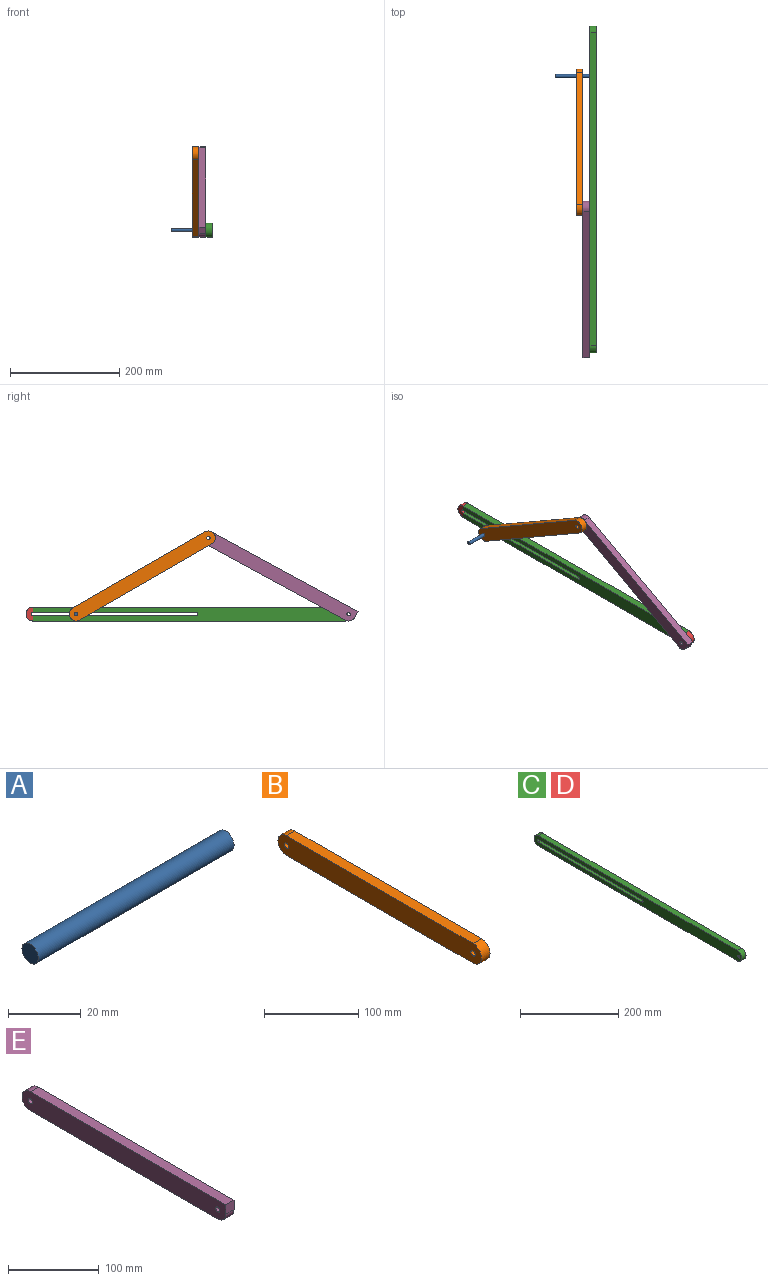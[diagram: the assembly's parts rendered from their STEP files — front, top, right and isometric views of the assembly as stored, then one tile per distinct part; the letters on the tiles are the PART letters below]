
ASSEMBLY  parts=5 mates=4
PART A: 3 faces, bbox 76.2x6.4x6.4 mm
  f0: cylinder r=3.17mm len=76.2mm, axis (-1,0,0), area 1520.1mm2, adj f1,f2
  f1: plane 6.35x6.35mm, normal (1,0,0), area 31.7mm2, adj f0
  f2: plane 6.35x6.35mm, normal (-1,0,0), area 31.7mm2, adj f0
PART B: 8 faces, bbox 12.7x304.8x25.4 mm
  f0: plane 279.4x12.7mm, normal (0,0,-1), area 3548.4mm2, adj f4,f5,f6,f7
  f1: cylinder r=3.17mm len=12.7mm, axis (-1,0,0), area 253.4mm2, adj f4,f5
  f2: plane 279.4x12.7mm, normal (0,0,1), area 3548.4mm2, adj f4,f5,f6,f7
  f3: cylinder r=3.17mm len=12.7mm, axis (-1,0,0), area 253.4mm2, adj f4,f5
  f4: plane 304.8x25.4mm, normal (1,0,0), area 7540.1mm2, adj f0,f1,f2,f3,f6,f7
  f5: plane 304.8x25.4mm, normal (-1,0,0), area 7540.1mm2, adj f0,f1,f2,f3,f6,f7
  f6: cylinder r=12.7mm len=25.4mm, axis (-1,0,0), area 506.7mm2, adj f0,f2,f4,f5
  f7: cylinder r=12.7mm len=25.4mm, axis (-1,0,0), area 506.7mm2, adj f0,f2,f4,f5
PART C: 11 faces, bbox 12.7x598.5x25.4 mm
  f0: plane 298.45x12.7mm, normal (0,0,1), area 3790.3mm2, adj f1,f4,f7,f8
  f1: cylinder r=3.17mm len=12.7mm, axis (1,0,0), area 126.7mm2, adj f0,f2,f7,f8
  f2: plane 298.45x12.7mm, normal (0,0,-1), area 3790.3mm2, adj f1,f4,f7,f8
  f3: plane 573.1x12.7mm, normal (0,0,-1), area 7278.4mm2, adj f7,f8,f9,f10
  f4: cylinder r=3.17mm len=12.7mm, axis (1,0,0), area 126.7mm2, adj f0,f2,f7,f8
  f5: plane 573.1x12.7mm, normal (0,0,1), area 7278.4mm2, adj f7,f8,f9,f10
  f6: cylinder r=3.17mm len=12.7mm, axis (1,0,0), area 253.4mm2, adj f7,f8
  f7: plane 598.5x25.4mm, normal (-1,0,0), area 13105mm2, adj f0,f1,f2,f3,f4,f5,f6,f9
  f8: plane 598.5x25.4mm, normal (1,0,0), area 13105mm2, adj f0,f1,f2,f3,f4,f5,f6,f9
  f9: cylinder r=12.7mm len=25.4mm, axis (-1,0,0), area 506.7mm2, adj f3,f5,f7,f8
  f10: cylinder r=12.7mm len=25.4mm, axis (-1,0,0), area 506.7mm2, adj f3,f5,f7,f8
PART D: same geometry as C
PART E: 9 faces, bbox 12.7x317.5x25.4 mm
  f0: plane 12.7x12.7mm, normal (0,-1,0), area 161.3mm2, adj f3,f5,f6,f7
  f1: plane 292.1x12.7mm, normal (0,0,-1), area 3709.7mm2, adj f5,f6,f7,f8
  f2: cylinder r=3.17mm len=12.7mm, axis (-1,0,0), area 253.4mm2, adj f5,f6
  f3: plane 304.8x12.7mm, normal (0,0,1), area 3871mm2, adj f0,f5,f6,f8
  f4: cylinder r=3.17mm len=12.7mm, axis (-1,0,0), area 253.4mm2, adj f5,f6
  f5: plane 317.5x25.4mm, normal (1,0,0), area 7897.3mm2, adj f0,f1,f2,f3,f4,f7,f8
  f6: plane 317.5x25.4mm, normal (-1,0,0), area 7897.3mm2, adj f0,f1,f2,f3,f4,f7,f8
  f7: cylinder r=12.7mm len=12.7mm, axis (-1,0,0), area 253.4mm2, adj f0,f1,f5,f6
  f8: cylinder r=12.7mm len=25.4mm, axis (1,0,0), area 506.7mm2, adj f1,f3,f5,f6
PLACE A rot(axis=(1,0,0),160.7deg) t=(-492.51,462.77,-106.32)mm
PLACE B rot(axis=(0,-0.26,-0.97),180deg) t=(447.29,209.62,9.04)mm
PLACE C t=(-454.41,-3.36,10.73)mm
PLACE D t=(-454.41,-3.36,10.73)mm fixed
PLACE E rot(axis=(1,0,0),28.5deg) t=(-479.81,-44.88,148.67)mm
MATE revolute A.f0 <-> B.f3  axis (-1,0,0) through (-73.41,203.28,-1.97)mm
MATE revolute E.f4 <-> D.f6  axis (1,0,0) through (-9.91,-295.46,-1.97)mm
MATE pin_slot A.f0 <-> D.f4  axis (-1,0,0) through (2.79,203.28,-1.97)mm
MATE revolute E.f2 <-> B.f1  axis (-1,0,0) through (-22.61,-38.82,137.51)mm
